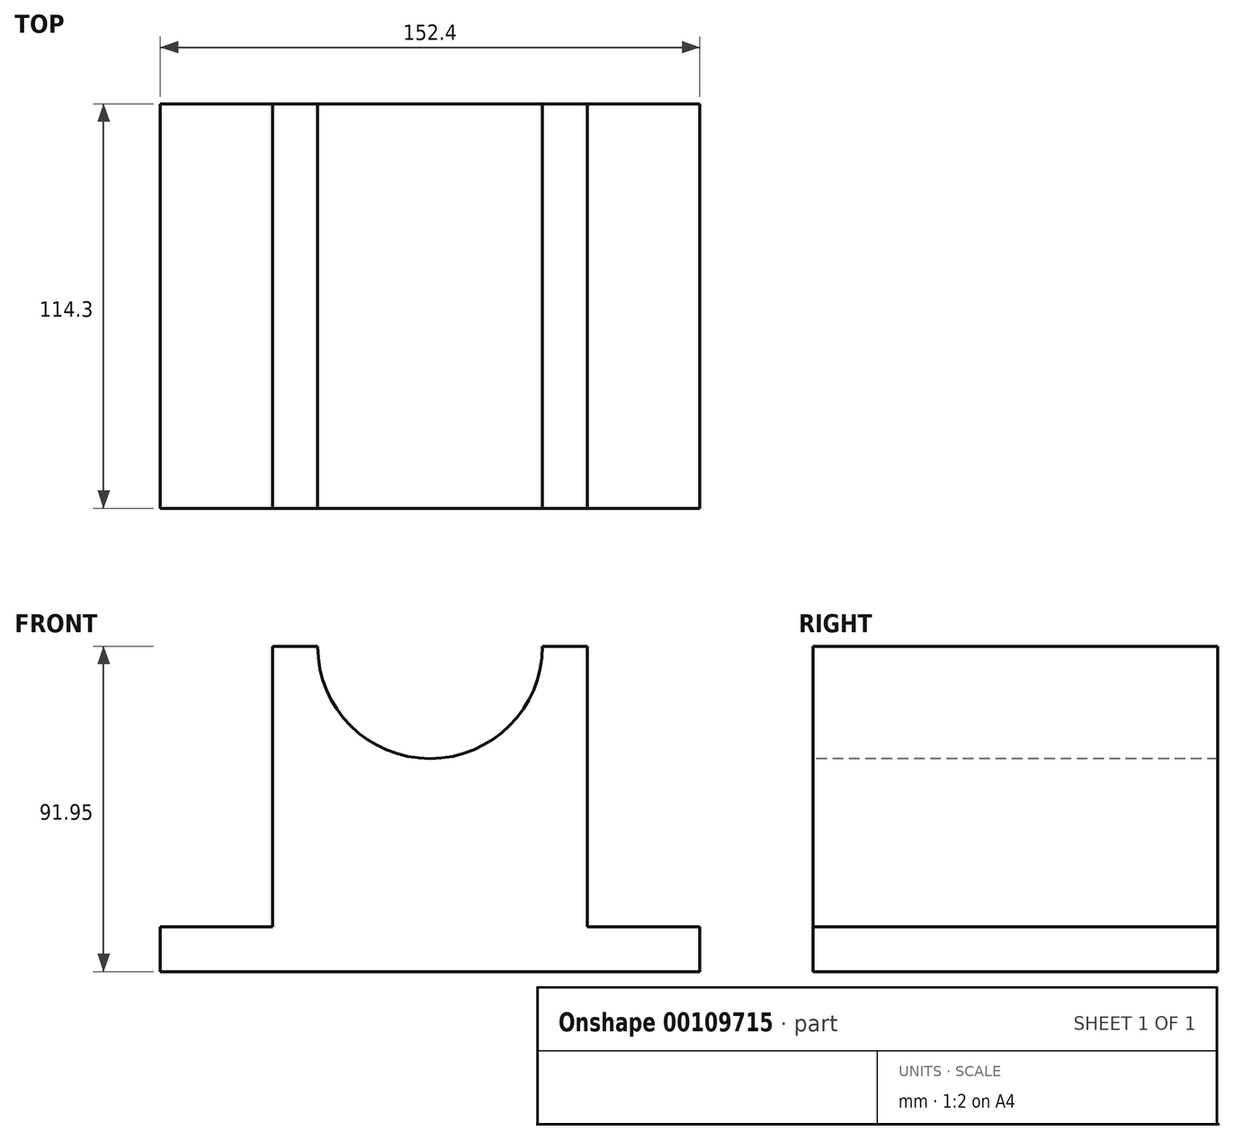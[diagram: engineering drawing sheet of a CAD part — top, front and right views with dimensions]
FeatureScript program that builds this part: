
annotation { "Feature Type Name" : "Feature", "Feature Type Description" : "" }
export const myFeature = defineFeature(function(context is Context, id is Id, definition is map)
    precondition{}
    {
        {
            var Q0;
            Q0=qCreatedBy(makeId("Top.planeOp"),FACE);
            var sketch = newSketch(context, id + "F0", { "sketchPlane" : qUnion([Q0])});
            skLineSegment(sketch, "E0.bottom", {"start": v(76.2, -57.15) * mm, "end": v(-76.2, -57.15) * mm});
            skLineSegment(sketch, "E0.top", {"start": v(76.2, 57.15) * mm, "end": v(-76.2, 57.15) * mm});
            skLineSegment(sketch, "E0.left", {"start": v(76.2, -57.15) * mm, "end": v(76.2, 57.15) * mm});
            skLineSegment(sketch, "E0.right", {"start": v(-76.2, -57.15) * mm, "end": v(-76.2, 57.15) * mm});
            skPoint(sketch, "E0.middle", {"position": v(0, 0) * mm});
            skSolve(sketch);
        }
        {
            var Q0;
            Q0=makeQuery(id+"F0.imprint","IMPRINT",FACE,{"disambiguationData":[TD([[makeQuery(id+"F0.imprint","IMPRINT",EDGE,{"derivedFrom":sQuery(id+"F0.wireOp",EDGE,"E0.bottom")}),-1.0]])]});
            extrude(context, id + "F1", {"entities" : qUnion([Q0]), "depth" : 91.95 * mm});
        }
        {
            var Q0;
            Q0=makeQuery(id+"F1.opExtrude","SWEPT_FACE",FACE,{"disambiguationData":[OSD([sQuery(id+"F0.wireOp",EDGE,"E0.bottom")])]});
            var sketch = newSketch(context, id + "F2", { "sketchPlane" : qUnion([Q0])});
            skArc(sketch, "E1", {"start": v(27.53, 107.77) * mm, "mid": v(-30.68, 83.76) * mm, "end": v(31.75, 91.95) * mm});
            skSolve(sketch);
        }
        {
            var Q0;
            {var subQ0=sQuery(id+"F2.wireOp",EDGE,"E1");var subQ1=makeQuery(id+"F1.opExtrude","CAP_EDGE",EDGE,{"disambiguationData":[OSD([sQuery(id+"F0.wireOp",EDGE,"E0.bottom")])],"isStart":false});var subQ2=makeQuery(id+"F2.imprint","INTERSECT",VERTEX,{"disambiguationData":[OD(0.0)],"derivedFrom":[subQ1,subQ0]});Q0=makeQuery(id+"F2.imprint","IMPRINT",FACE,{"disambiguationData":[TD([[makeQuery(id+"F2.imprint","IMPRINT",EDGE,{"disambiguationData":[TD([[subQ2,1.0]])],"derivedFrom":subQ0}),1.0]])]});}
            extrude(context, id + "F3", {"entities" : qUnion([Q0]), "operationType" : NewBodyOperationType.REMOVE, "oppositeDirection" : true, "depth" : 175.39 * mm});
        }
        {
            var Q0;
            {var subQ0=sQuery(id+"F0.wireOp",EDGE,"E0.bottom");var subQ1=sQuery(id+"F0.wireOp",EDGE,"E0.top");var subQ2=sQuery(id+"F0.wireOp",EDGE,"E0.left");Q0=makeQuery(id+"F3.boolean.opBoolean","SPLIT",FACE,{"disambiguationData":[TD([makeQuery(id+"F1.opExtrude","SWEPT_FACE",FACE,{"disambiguationData":[OSD([subQ2])]})])],"derivedFrom":makeQuery(id+"F1.opExtrude","CAP_FACE",FACE,{"disambiguationData":[OSD([subQ0,subQ1,subQ2,sQuery(id+"F0.wireOp",EDGE,"E0.right")])],"isStart":false})});}
            var sketch = newSketch(context, id + "F4", { "sketchPlane" : qUnion([Q0])});
            skLineSegment(sketch, "E2", {"start": v(31.75, -57.15) * mm, "end": v(44.45, -57.15) * mm});
            skLineSegment(sketch, "E3", {"start": v(44.45, -57.15) * mm, "end": v(44.45, 57.15) * mm});
            skSolve(sketch);
        }
        {
            var Q0;
            {var subQ0=sQuery(id+"F4.wireOp",EDGE,"E3");Q0=makeQuery(id+"F4.imprint","IMPRINT",FACE,{"disambiguationData":[TD([[makeQuery(id+"F4.imprint","IMPRINT",EDGE,{"derivedFrom":subQ0}),-1.0]])]});}
            extrude(context, id + "F5", {"entities" : qUnion([Q0]), "operationType" : NewBodyOperationType.REMOVE, "oppositeDirection" : true, "depth" : 79.25 * mm});
        }
        {
            var Q0;
            {var subQ0=sQuery(id+"F0.wireOp",EDGE,"E0.bottom");var subQ1=sQuery(id+"F0.wireOp",EDGE,"E0.top");var subQ2=sQuery(id+"F0.wireOp",EDGE,"E0.right");Q0=makeQuery(id+"F3.boolean.opBoolean","SPLIT",FACE,{"disambiguationData":[TD([makeQuery(id+"F1.opExtrude","SWEPT_FACE",FACE,{"disambiguationData":[OSD([subQ2])]})])],"derivedFrom":makeQuery(id+"F1.opExtrude","CAP_FACE",FACE,{"disambiguationData":[OSD([subQ0,subQ1,sQuery(id+"F0.wireOp",EDGE,"E0.left"),subQ2])],"isStart":false})});}
            var sketch = newSketch(context, id + "F6", { "sketchPlane" : qUnion([Q0])});
            skLineSegment(sketch, "E4", {"start": v(-31.75, -57.15) * mm, "end": v(-44.45, -57.15) * mm});
            skLineSegment(sketch, "E5", {"start": v(-44.45, -57.15) * mm, "end": v(-44.45, 57.15) * mm});
            skSolve(sketch);
        }
        {
            var Q0;
            {var subQ0=sQuery(id+"F6.wireOp",EDGE,"E5");Q0=makeQuery(id+"F6.imprint","IMPRINT",FACE,{"disambiguationData":[TD([[makeQuery(id+"F6.imprint","IMPRINT",EDGE,{"derivedFrom":subQ0}),1.0]])]});}
            extrude(context, id + "F7", {"entities" : qUnion([Q0]), "operationType" : NewBodyOperationType.REMOVE, "oppositeDirection" : true, "depth" : 79.25 * mm});
        }
    });
